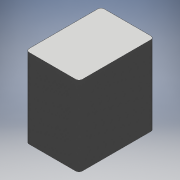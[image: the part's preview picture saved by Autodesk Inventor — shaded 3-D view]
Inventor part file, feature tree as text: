
AUTODESK INVENTOR PART (.ipt)
format: ipt  version: 2018 (Build 220112000, 112)  size: 2,231,296 bytes
history: native  units: mm
features: extrude x1, pattern_linear x1, sketch x1
ambient origin geometry x8: Origin, YZ Plane, XZ Plane, XY Plane, X Axis, Y Axis, Z Axis, Center Point
bodies: Solid1 (feature_tree)
feature tree (3):
  extrude  "Extrusion1"  Depth=89.0mm
  pattern_linear  "Rectangular Pattern1"  Spacing1=4.0mm  [1 undecoded]
  sketch  "Sketch1"  dims[d0=63.0mm d1=89.0mm d2=4.0mm d3=0.27mm d4=0.0mm d5=3290.0mm d7=93.73mm]
note: 1 required parameter value undecoded (feature->parameter linkage not recoverable at this tier; creation-order binding heuristic only, values carry confidence <= 0.55)
